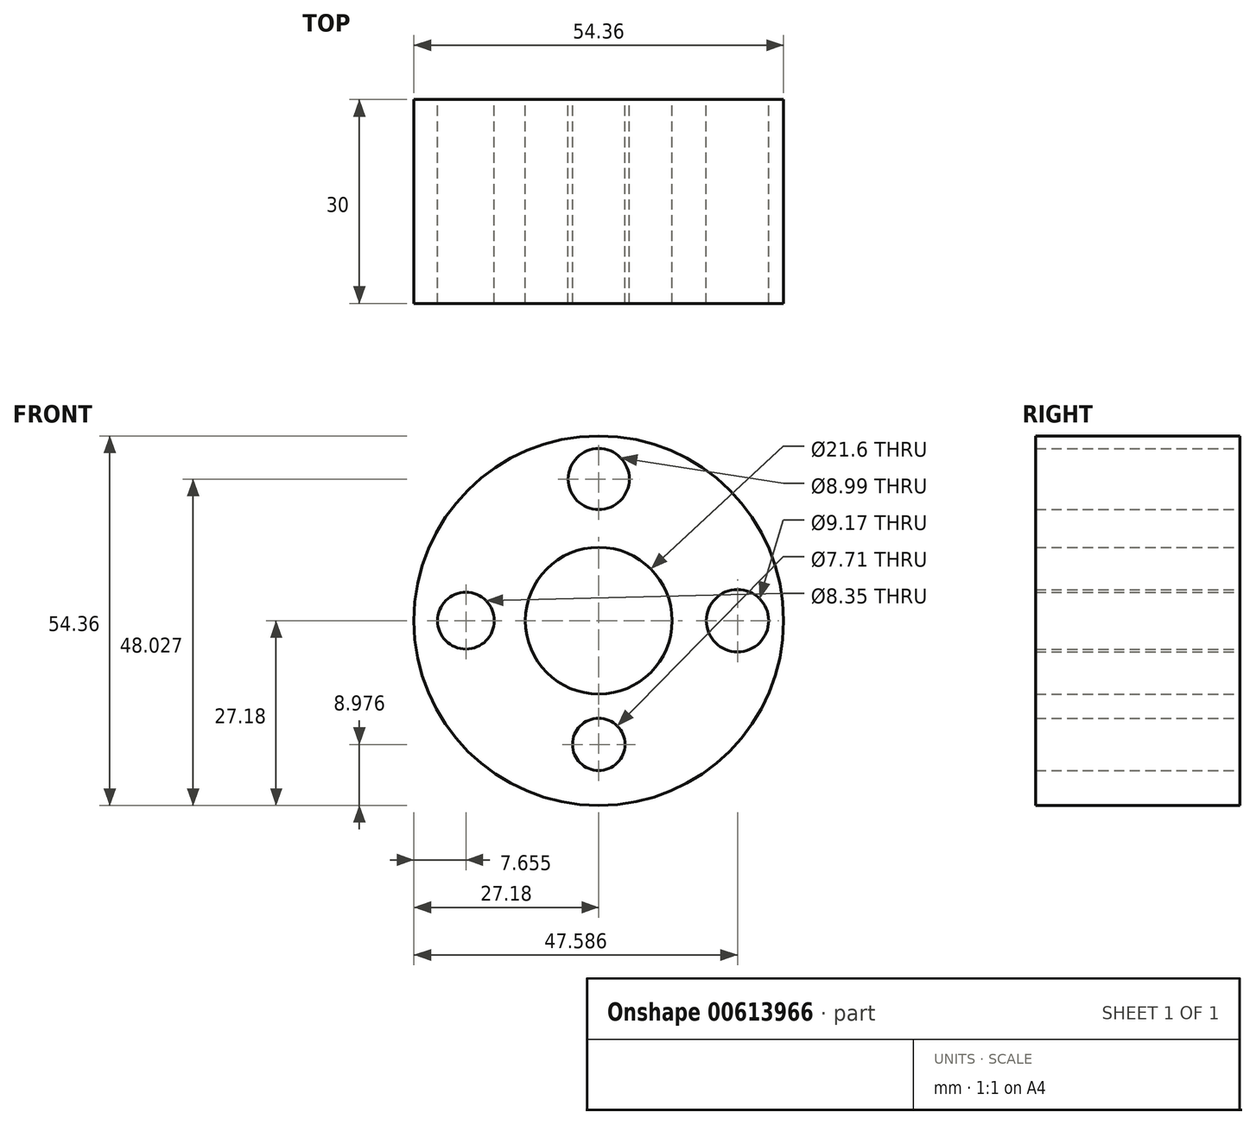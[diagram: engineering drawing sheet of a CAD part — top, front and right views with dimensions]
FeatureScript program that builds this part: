
annotation { "Feature Type Name" : "Feature", "Feature Type Description" : "" }
export const myFeature = defineFeature(function(context is Context, id is Id, definition is map)
    precondition{}
    {
        {
            var Q0;
            Q0=qCreatedBy(makeId("Front.planeOp"),FACE);
            var sketch = newSketch(context, id + "F0", { "sketchPlane" : qUnion([Q0])});
            skCircle(sketch, "E0", {"center": v(0, 0) * mm, "radius": 27.18 * mm});
            skCircle(sketch, "E1", {"center": v(0, 0) * mm, "radius": 10.8 * mm});
            skCircle(sketch, "E2", {"center": v(0, 0) * mm, "radius": 6.17 * mm});
            skCircle(sketch, "E3", {"center": v(0, 20.85) * mm, "radius": 4.5 * mm});
            skCircle(sketch, "E4", {"center": v(0, 20.85) * mm, "radius": 1.8 * mm});
            skCircle(sketch, "E5", {"center": v(20.4, 0) * mm, "radius": 4.59 * mm});
            skCircle(sketch, "E6", {"center": v(20.4, 0) * mm, "radius": 2.12 * mm});
            skCircle(sketch, "E7", {"center": v(0, -18.2) * mm, "radius": 3.85 * mm});
            skCircle(sketch, "E8", {"center": v(0, -18.2) * mm, "radius": 1.93 * mm});
            skCircle(sketch, "E9", {"center": v(-19.53, 0) * mm, "radius": 4.17 * mm});
            skCircle(sketch, "E10", {"center": v(-19.53, 0) * mm, "radius": 2.24 * mm});
            skSolve(sketch);
        }
        {
            var Q0;
            Q0 = qSketchRegion(id + "F0", true);
            extrude(context, id + "F1", {"entities" : qUnion([Q0]), "depth" : 30 * mm, "offsetDistance" : 25 * mm});
        }
    });
